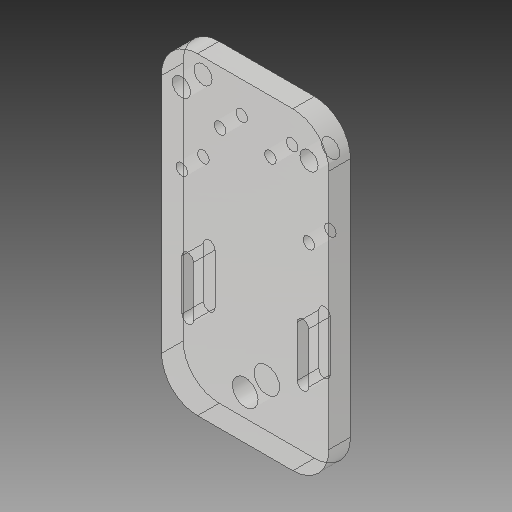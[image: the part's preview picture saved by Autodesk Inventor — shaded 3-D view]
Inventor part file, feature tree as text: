
AUTODESK INVENTOR PART (.ipt)
format: ipt  version: 2017 (Build 210142000, 142)  size: 182,272 bytes
history: native  units: mm
features: other x3, sketch x2
ambient origin geometry x8: Origin, YZ Plane, XZ Plane, XY Plane, X Axis, Y Axis, Z Axis, Center Point
bodies: Solid1 (feature_tree)
feature tree (5):
  other  "Hotend Front Plate revised_MIR.ipt"
  other  "Solid1::Hotend Front Plate revised_MIR.ipt"
  other  "TaggingFeature1"
  sketch  "Sketch1"  dims[d0=10.0mm]
  sketch  "Sketch2"
